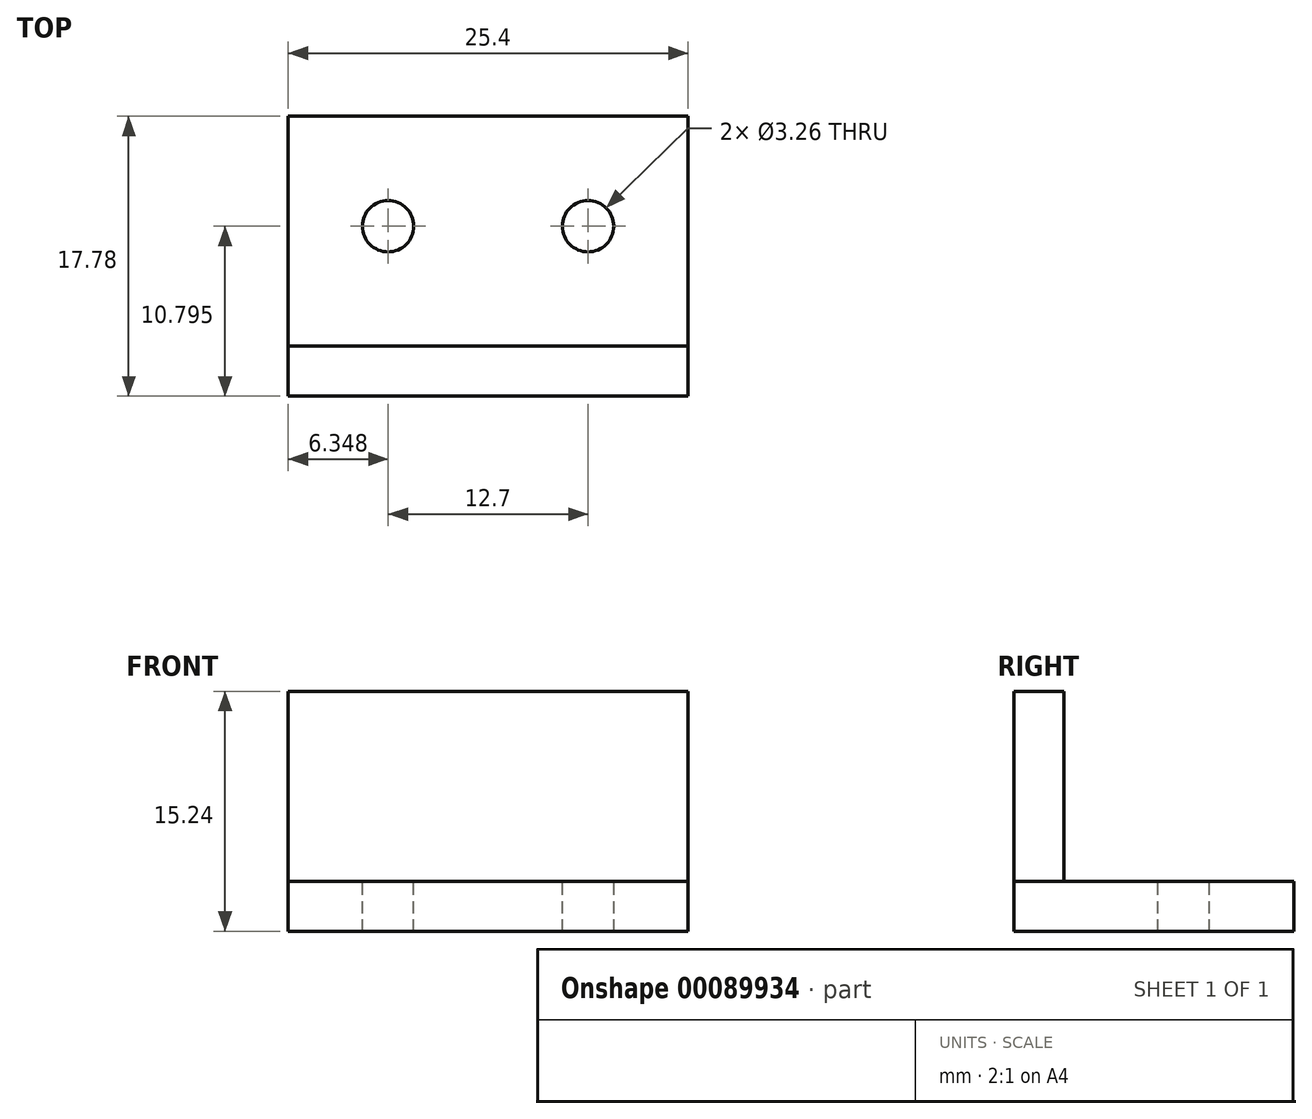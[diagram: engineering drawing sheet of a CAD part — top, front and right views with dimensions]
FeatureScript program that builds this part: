
annotation { "Feature Type Name" : "Feature", "Feature Type Description" : "" }
export const myFeature = defineFeature(function(context is Context, id is Id, definition is map)
    precondition{}
    {
        {
            var Q0;
            Q0=qCreatedBy(makeId("Front.planeOp"),FACE);
            var sketch = newSketch(context, id + "F0", { "sketchPlane" : qUnion([Q0])});
            skLineSegment(sketch, "E0.bottom", {"start": v(1.12, 0) * mm, "end": v(26.52, 0) * mm});
            skLineSegment(sketch, "E0.top", {"start": v(1.12, 3.18) * mm, "end": v(26.52, 3.18) * mm});
            skLineSegment(sketch, "E0.left", {"start": v(1.12, 0) * mm, "end": v(1.12, 3.18) * mm});
            skLineSegment(sketch, "E0.right", {"start": v(26.52, 0) * mm, "end": v(26.52, 3.18) * mm});
            skSolve(sketch);
        }
        {
            var Q0;
            Q0=makeQuery(id+"F0.imprint","IMPRINT",FACE,{"disambiguationData":[TD([[makeQuery(id+"F0.imprint","IMPRINT",EDGE,{"derivedFrom":sQuery(id+"F0.wireOp",EDGE,"E0.bottom")}),1.0]])]});
            extrude(context, id + "F1", {"entities" : qUnion([Q0]), "depth" : 25.4 * mm});
        }
        {
            var Q0;
            Q0=makeQuery(id+"F1.opExtrude","SWEPT_FACE",FACE,{"disambiguationData":[OSD([sQuery(id+"F0.wireOp",EDGE,"E0.right")])]});
            var sketch = newSketch(context, id + "F2", { "sketchPlane" : qUnion([Q0])});
            skLineSegment(sketch, "E1.bottom", {"start": v(-25.4, 0) * mm, "end": v(-22.23, 0) * mm});
            skLineSegment(sketch, "E1.top", {"start": v(-25.4, 18.41) * mm, "end": v(-22.23, 18.41) * mm});
            skLineSegment(sketch, "E1.left", {"start": v(-25.4, 0) * mm, "end": v(-25.4, 18.41) * mm});
            skLineSegment(sketch, "E1.right", {"start": v(-22.23, 0) * mm, "end": v(-22.23, 18.41) * mm});
            skSolve(sketch);
        }
        {
            var Q0;
            {var subQ0=sQuery(id+"F2.wireOp",EDGE,"E1.top");Q0=makeQuery(id+"F2.imprint","IMPRINT",FACE,{"disambiguationData":[TD([[makeQuery(id+"F2.imprint","IMPRINT",EDGE,{"derivedFrom":subQ0}),-1.0]])]});}
            extrude(context, id + "F3", {"entities" : qUnion([Q0]), "oppositeDirection" : true, "depth" : 25.4 * mm});
        }
        {
            var Q0;
            Q0=makeQuery(id+"F3.opExtrude","SWEPT_FACE",FACE,{"disambiguationData":[OSD([sQuery(id+"F2.wireOp",EDGE,"E1.right")])]});
            var sketch = newSketch(context, id + "F4", { "sketchPlane" : qUnion([Q0])});
            skLineSegment(sketch, "E2", {"start": v(-26.52, 10.8) * mm, "end": v(-1.12, 10.8) * mm});
            skLineSegment(sketch, "E3", {"start": v(-13.82, 10.8) * mm, "end": v(-26.52, 10.8) * mm});
            skLineSegment(sketch, "E4", {"start": v(-13.82, 10.8) * mm, "end": v(-1.12, 10.8) * mm});
            skPoint(sketch, "E5", {"position": v(-20.17, 10.8) * mm});
            skPoint(sketch, "E6", {"position": v(-7.47, 10.8) * mm});
            skSolve(sketch);
        }
        {
            var Q0;
            Q0=sQuery(id+"F4.wireOp",VERTEX,"E5");
            var Q1;
            Q1=sQuery(id+"F4.wireOp",VERTEX,"E6");
            var Q2;
            Q2=makeQuery(id+"F1.opExtrude","SWEPT_BODY",BODY,{"disambiguationData":[OSD([sQuery(id+"F0.wireOp",EDGE,"E0.bottom"),sQuery(id+"F0.wireOp",EDGE,"E0.top"),sQuery(id+"F0.wireOp",EDGE,"E0.left"),sQuery(id+"F0.wireOp",EDGE,"E0.right")])]});
            hole(context, id + "F5", {"style" : HoleStyle.SIMPLE, "endStyle" : HoleEndStyle.BLIND, "standardTappedOrClearance" : lookupTablePath({ "standard" : "ANSI", "fit" : "Normal (ASME)", "size" : "#4", "type" : "Clearance" }), "standardBlindInLast" : lookupTablePath({ "fit" : "Free", "standard" : "ANSI", "size" : "#4", "type" : "Clearance" }), "holeDiameter" : 3.26 * mm, "holeDepth" : 12.7 * mm, "locations" : qUnion([Q0, Q1]), "scope" : qUnion([Q2])});
        }
        {
            var Q0;
            Q0=makeQuery(id+"F1.opExtrude","SWEPT_FACE",FACE,{"disambiguationData":[OSD([sQuery(id+"F0.wireOp",EDGE,"E0.top")])]});
            var sketch = newSketch(context, id + "F6", { "sketchPlane" : qUnion([Q0])});
            skLineSegment(sketch, "E7", {"start": v(13.82, -22.23) * mm, "end": v(13.82, -11.11) * mm});
            skPoint(sketch, "E8", {"position": v(7.47, -14.6) * mm});
            skPoint(sketch, "E9", {"position": v(20.17, -14.6) * mm});
            skSolve(sketch);
        }
        {
            var Q0;
            Q0=sQuery(id+"F6.wireOp",VERTEX,"E8");
            var Q1;
            Q1=sQuery(id+"F6.wireOp",VERTEX,"E9");
            var Q2;
            Q2=makeQuery(id+"F1.opExtrude","SWEPT_BODY",BODY,{"disambiguationData":[OSD([sQuery(id+"F0.wireOp",EDGE,"E0.bottom"),sQuery(id+"F0.wireOp",EDGE,"E0.top"),sQuery(id+"F0.wireOp",EDGE,"E0.left"),sQuery(id+"F0.wireOp",EDGE,"E0.right")])]});
            hole(context, id + "F7", {"style" : HoleStyle.SIMPLE, "endStyle" : HoleEndStyle.BLIND, "standardTappedOrClearance" : lookupTablePath({ "standard" : "ANSI", "fit" : "Normal (ASME)", "size" : "#4", "type" : "Clearance" }), "standardBlindInLast" : lookupTablePath({ "fit" : "Free", "standard" : "ANSI", "size" : "#4", "type" : "Clearance" }), "holeDiameter" : 3.26 * mm, "holeDepth" : 12.7 * mm, "locations" : qUnion([Q0, Q1]), "scope" : qUnion([Q2])});
        }
        {
            var Q0;
            Q0=makeQuery(id+"F3.opExtrude","SWEPT_FACE",FACE,{"disambiguationData":[OSD([sQuery(id+"F2.wireOp",EDGE,"E1.right")])]});
            var sketch = newSketch(context, id + "F8", { "sketchPlane" : qUnion([Q0])});
            skLineSegment(sketch, "E10.bottom", {"start": v(-26.52, 18.42) * mm, "end": v(-1.12, 18.42) * mm});
            skLineSegment(sketch, "E10.top", {"start": v(-26.52, 15.24) * mm, "end": v(-1.12, 15.24) * mm});
            skLineSegment(sketch, "E10.left", {"start": v(-26.52, 18.42) * mm, "end": v(-26.52, 15.24) * mm});
            skLineSegment(sketch, "E10.right", {"start": v(-1.12, 18.42) * mm, "end": v(-1.12, 15.24) * mm});
            skSolve(sketch);
        }
        {
            var Q0;
            Q0=makeQuery(id+"F8.imprint","IMPRINT",FACE,{"disambiguationData":[TD([[makeQuery(id+"F8.imprint","IMPRINT",EDGE,{"derivedFrom":sQuery(id+"F8.wireOp",EDGE,"E10.bottom")}),1.0]])]});
            extrude(context, id + "F9", {"entities" : qUnion([Q0]), "operationType" : NewBodyOperationType.REMOVE, "endBound" : BoundingType.THROUGH_ALL, "oppositeDirection" : true, "depth" : 25.4 * mm});
        }
        {
            var Q0;
            Q0=makeQuery(id+"F1.opExtrude","SWEPT_FACE",FACE,{"disambiguationData":[OSD([sQuery(id+"F0.wireOp",EDGE,"E0.top")])]});
            var sketch = newSketch(context, id + "F10", { "sketchPlane" : qUnion([Q0])});
            skLineSegment(sketch, "E11", {"start": v(1.12, 0) * mm, "end": v(13.82, 0) * mm});
            skLineSegment(sketch, "E12.bottom", {"start": v(0, 0) * mm, "end": v(26.52, 0) * mm});
            skLineSegment(sketch, "E12.top", {"start": v(0, -7.62) * mm, "end": v(26.52, -7.62) * mm});
            skLineSegment(sketch, "E12.left", {"start": v(0, 0) * mm, "end": v(0, -7.62) * mm});
            skLineSegment(sketch, "E12.right", {"start": v(26.52, 0) * mm, "end": v(26.52, -7.62) * mm});
            skSolve(sketch);
        }
        {
            var Q0;
            {var subQ4=sQuery(id+"F10.wireOp",EDGE,"E12.right");Q0=makeQuery(id+"F10.imprint","IMPRINT",FACE,{"disambiguationData":[TD([[makeQuery(id+"F10.imprint","IMPRINT",EDGE,{"derivedFrom":subQ4}),1.0]])]});}
            extrude(context, id + "F11", {"entities" : qUnion([Q0]), "operationType" : NewBodyOperationType.REMOVE, "endBound" : BoundingType.THROUGH_ALL, "oppositeDirection" : true, "depth" : 25.4 * mm});
        }
    });
